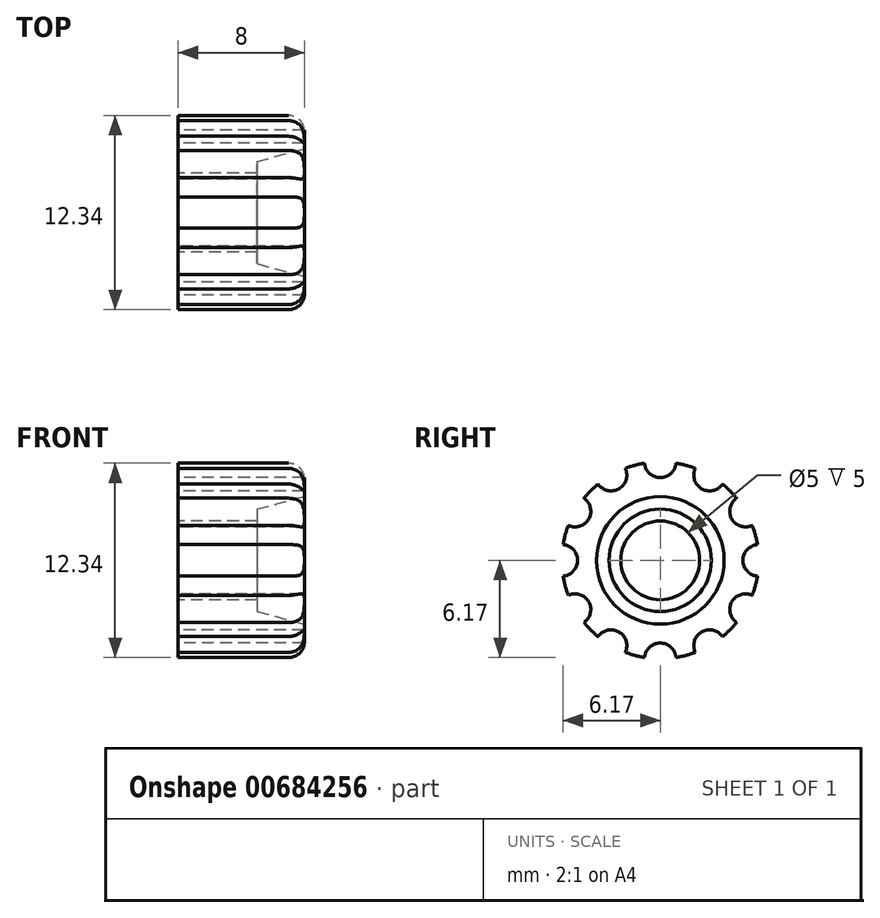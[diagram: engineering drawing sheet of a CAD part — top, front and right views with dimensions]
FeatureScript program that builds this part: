
annotation { "Feature Type Name" : "Feature", "Feature Type Description" : "" }
export const myFeature = defineFeature(function(context is Context, id is Id, definition is map)
    precondition{}
    {
        {
            var Q0;
            Q0=qCreatedBy(makeId("Front.planeOp"),FACE);
            var sketch = newSketch(context, id + "F0", { "sketchPlane" : qUnion([Q0])});
            skLineSegment(sketch, "E0", {"start": v(0, 2.5) * mm, "end": v(5, 2.5) * mm});
            skLineSegment(sketch, "E1", {"start": v(0, 4.05) * mm, "end": v(0, 2.5) * mm});
            skLineSegment(sketch, "E2", {"start": v(5, 2.5) * mm, "end": v(5, 3.25) * mm});
            skLineSegment(sketch, "E3", {"start": v(5, 3.25) * mm, "end": v(8, 4.05) * mm});
            skLineSegment(sketch, "E4", {"start": v(-4.39, 0) * mm, "end": v(12.33, 0) * mm});
            skLineSegment(sketch, "E5", {"start": v(0, 4.05) * mm, "end": v(8, 4.05) * mm});
            skSolve(sketch);
        }
        {
            var Q0;
            Q0=makeQuery(id+"F0.imprint","IMPRINT",FACE,{"disambiguationData":[TD([[makeQuery(id+"F0.imprint","IMPRINT",EDGE,{"derivedFrom":sQuery(id+"F0.wireOp",EDGE,"E0")}),1.0]])]});
            var Q1;
            Q1=sQuery(id+"F0.wireOp",EDGE,"E4");
            revolve(context, id + "F1", {"entities" : qUnion([Q0]), "axis" : qUnion([Q1]), "revolveType" : RevolveType.FULL});
        }
        {
            var Q0;
            Q0=qCreatedBy(makeId("Right.planeOp"),FACE);
            var sketch = newSketch(context, id + "F2", { "sketchPlane" : qUnion([Q0])});
            skArc(sketch, "E6", {"start": v(-3.95, 4.84) * mm, "mid": v(-4.42, 4.42) * mm, "end": v(-4.84, 3.95) * mm});
            skArc(sketch, "E7", {"start": v(-1, 6.17) * mm, "mid": v(0, 5.25) * mm, "end": v(1, 6.17) * mm});
            skArc(sketch, "E8.1.0", {"start": v(-3.95, 4.84) * mm, "mid": v(-2.63, 4.55) * mm, "end": v(-2.22, 5.84) * mm});
            skArc(sketch, "E8.2.0", {"start": v(-5.84, 2.22) * mm, "mid": v(-4.55, 2.62) * mm, "end": v(-4.84, 3.95) * mm});
            skArc(sketch, "E8.3.0", {"start": v(-6.17, -1) * mm, "mid": v(-5.25, 0) * mm, "end": v(-6.17, 1) * mm});
            skArc(sketch, "E8.4.0", {"start": v(-4.84, -3.95) * mm, "mid": v(-4.55, -2.62) * mm, "end": v(-5.84, -2.22) * mm});
            skArc(sketch, "E8.5.0", {"start": v(-2.22, -5.84) * mm, "mid": v(-2.62, -4.55) * mm, "end": v(-3.95, -4.84) * mm});
            skArc(sketch, "E8.6.0", {"start": v(1, -6.17) * mm, "mid": v(0, -5.25) * mm, "end": v(-1, -6.17) * mm});
            skArc(sketch, "E8.7.0", {"start": v(3.95, -4.84) * mm, "mid": v(2.62, -4.55) * mm, "end": v(2.22, -5.84) * mm});
            skArc(sketch, "E8.8.0", {"start": v(5.84, -2.22) * mm, "mid": v(4.55, -2.63) * mm, "end": v(4.84, -3.95) * mm});
            skArc(sketch, "E8.9.0", {"start": v(6.17, 1) * mm, "mid": v(5.25, 0) * mm, "end": v(6.17, -1) * mm});
            skArc(sketch, "E8.10.0", {"start": v(4.84, 3.95) * mm, "mid": v(4.55, 2.63) * mm, "end": v(5.84, 2.22) * mm});
            skArc(sketch, "E8.11.0", {"start": v(2.22, 5.84) * mm, "mid": v(2.63, 4.55) * mm, "end": v(3.95, 4.84) * mm});
            skArc(sketch, "E9.trimOffspring", {"start": v(-5.84, 2.22) * mm, "mid": v(-6.04, 1.62) * mm, "end": v(-6.17, 1) * mm});
            skArc(sketch, "E10.trimOffspring", {"start": v(-6.17, -1) * mm, "mid": v(-6.04, -1.62) * mm, "end": v(-5.84, -2.22) * mm});
            skArc(sketch, "E11.trimOffspring", {"start": v(-4.84, -3.95) * mm, "mid": v(-4.42, -4.42) * mm, "end": v(-3.95, -4.84) * mm});
            skArc(sketch, "E12.trimOffspring", {"start": v(-2.22, -5.84) * mm, "mid": v(-1.62, -6.04) * mm, "end": v(-1, -6.17) * mm});
            skArc(sketch, "E13.trimOffspring", {"start": v(1, -6.17) * mm, "mid": v(1.62, -6.04) * mm, "end": v(2.22, -5.84) * mm});
            skArc(sketch, "E14.trimOffspring", {"start": v(3.95, -4.84) * mm, "mid": v(4.42, -4.42) * mm, "end": v(4.84, -3.95) * mm});
            skArc(sketch, "E15.trimOffspring", {"start": v(5.84, -2.22) * mm, "mid": v(6.04, -1.62) * mm, "end": v(6.17, -1) * mm});
            skArc(sketch, "E16.trimOffspring", {"start": v(6.17, 1) * mm, "mid": v(6.04, 1.62) * mm, "end": v(5.84, 2.22) * mm});
            skArc(sketch, "E17.trimOffspring", {"start": v(4.84, 3.95) * mm, "mid": v(4.42, 4.42) * mm, "end": v(3.95, 4.84) * mm});
            skArc(sketch, "E18.trimOffspring", {"start": v(2.22, 5.84) * mm, "mid": v(1.62, 6.04) * mm, "end": v(1, 6.17) * mm});
            skArc(sketch, "E19.trimOffspring", {"start": v(-1, 6.17) * mm, "mid": v(-1.62, 6.04) * mm, "end": v(-2.22, 5.84) * mm});
            skCircle(sketch, "E20.0", {"center": v(0, 0) * mm, "radius": 4.05 * mm});
            skSolve(sketch);
        }
        {
            var Q0;
            Q0=makeQuery(id+"F2.imprint","IMPRINT",FACE,{"disambiguationData":[TD([[makeQuery(id+"F2.imprint","IMPRINT",EDGE,{"derivedFrom":sQuery(id+"F2.wireOp",EDGE,"E6")}),1.0]])]});
            extrude(context, id + "F3", {"entities" : qUnion([Q0]), "operationType" : NewBodyOperationType.ADD, "depth" : 8 * mm, "offsetDistance" : 25 * mm});
        }
        {
            var Q0;
            Q0=makeQuery(id+"F3.opExtrude","CAP_EDGE",EDGE,{"disambiguationData":[OSD([sQuery(id+"F2.wireOp",EDGE,"E6")])],"isStart":false});
            var Q1;
            Q1=makeQuery(id+"F3.opExtrude","CAP_EDGE",EDGE,{"disambiguationData":[OSD([sQuery(id+"F2.wireOp",EDGE,"E19.trimOffspring")])],"isStart":false});
            var Q2;
            Q2=makeQuery(id+"F3.opExtrude","CAP_EDGE",EDGE,{"disambiguationData":[OSD([sQuery(id+"F2.wireOp",EDGE,"E18.trimOffspring")])],"isStart":false});
            var Q3;
            Q3=makeQuery(id+"F3.opExtrude","CAP_EDGE",EDGE,{"disambiguationData":[OSD([sQuery(id+"F2.wireOp",EDGE,"E17.trimOffspring")])],"isStart":false});
            var Q4;
            Q4=makeQuery(id+"F3.opExtrude","CAP_EDGE",EDGE,{"disambiguationData":[OSD([sQuery(id+"F2.wireOp",EDGE,"E16.trimOffspring")])],"isStart":false});
            var Q5;
            Q5=makeQuery(id+"F3.opExtrude","CAP_EDGE",EDGE,{"disambiguationData":[OSD([sQuery(id+"F2.wireOp",EDGE,"E15.trimOffspring")])],"isStart":false});
            var Q6;
            Q6=makeQuery(id+"F3.opExtrude","CAP_EDGE",EDGE,{"disambiguationData":[OSD([sQuery(id+"F2.wireOp",EDGE,"E14.trimOffspring")])],"isStart":false});
            var Q7;
            Q7=makeQuery(id+"F3.opExtrude","CAP_EDGE",EDGE,{"disambiguationData":[OSD([sQuery(id+"F2.wireOp",EDGE,"E13.trimOffspring")])],"isStart":false});
            var Q8;
            Q8=makeQuery(id+"F3.opExtrude","CAP_EDGE",EDGE,{"disambiguationData":[OSD([sQuery(id+"F2.wireOp",EDGE,"E12.trimOffspring")])],"isStart":false});
            var Q9;
            Q9=makeQuery(id+"F3.opExtrude","CAP_EDGE",EDGE,{"disambiguationData":[OSD([sQuery(id+"F2.wireOp",EDGE,"E11.trimOffspring")])],"isStart":false});
            var Q10;
            Q10=makeQuery(id+"F3.opExtrude","CAP_EDGE",EDGE,{"disambiguationData":[OSD([sQuery(id+"F2.wireOp",EDGE,"E10.trimOffspring")])],"isStart":false});
            var Q11;
            Q11=makeQuery(id+"F3.opExtrude","CAP_EDGE",EDGE,{"disambiguationData":[OSD([sQuery(id+"F2.wireOp",EDGE,"E9.trimOffspring")])],"isStart":false});
            fillet(context, id + "F4", {"entities" : qUnion([Q0, Q1, Q2, Q3, Q4, Q5, Q6, Q7, Q8, Q9, Q10, Q11]), "radius" : 1 * mm, "tangentPropagation" : true, "allowEdgeOverflow" : false});
        }
    });
